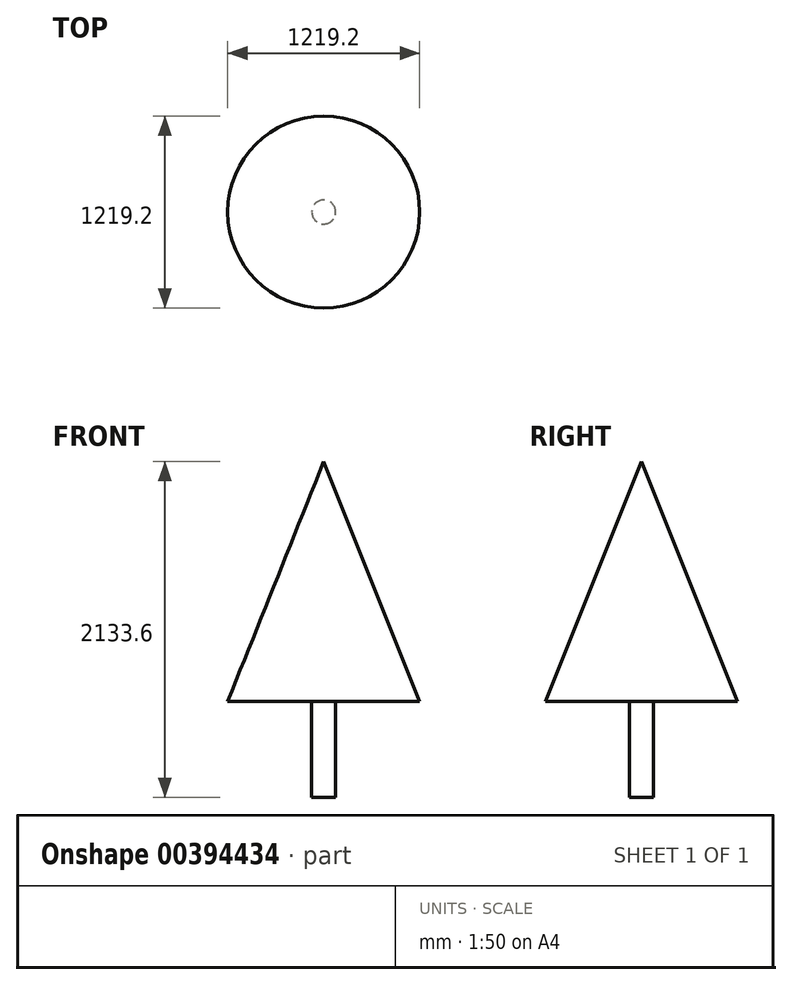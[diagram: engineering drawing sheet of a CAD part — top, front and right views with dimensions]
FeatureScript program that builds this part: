
annotation { "Feature Type Name" : "Feature", "Feature Type Description" : "" }
export const myFeature = defineFeature(function(context is Context, id is Id, definition is map)
    precondition{}
    {
        {
            var Q0;
            Q0=qCreatedBy(makeId("Top.planeOp"),FACE);
            var sketch = newSketch(context, id + "F0", { "sketchPlane" : qUnion([Q0])});
            skCircle(sketch, "E0", {"center": v(0, 0) * mm, "radius": 609.6 * mm});
            skSolve(sketch);
        }
        {
            var Q0;
            Q0=qCreatedBy(makeId("Front.planeOp"),FACE);
            var sketch = newSketch(context, id + "F1", { "sketchPlane" : qUnion([Q0])});
            skLineSegment(sketch, "E1", {"start": v(0, 0) * mm, "end": v(0, 1524) * mm});
            skSolve(sketch);
        }
        {
            var Q0;
            Q0=makeQuery(id+"F0.imprint","IMPRINT",FACE,{"disambiguationData":[TD([[makeQuery(id+"F0.imprint","IMPRINT",EDGE,{"derivedFrom":sQuery(id+"F0.wireOp",EDGE,"E0")}),1.0]])]});
            var Q1;
            Q1=sQuery(id+"F1.wireOp",VERTEX,"E1.end");
            loft(context, id + "F2", {"sheetProfilesArray" : [{ "sheetProfileEntities" : qUnion([Q0]) }, { "sheetProfileEntities" : qUnion([Q1]) }]});
        }
        {
            var Q0;
            Q0=makeQuery(id+"F2.opLoft","CAP_FACE",FACE,{"disambiguationData":[OSD([makeQuery(id+"F0.imprint","IMPRINT",FACE,{"disambiguationData":[TD([[makeQuery(id+"F0.imprint","IMPRINT",EDGE,{"derivedFrom":sQuery(id+"F0.wireOp",EDGE,"E0")}),1.0]])]})])],"isStart":true});
            var sketch = newSketch(context, id + "F3", { "sketchPlane" : qUnion([Q0])});
            skCircle(sketch, "E2", {"center": v(0, 0) * mm, "radius": 76.2 * mm});
            skSolve(sketch);
        }
        {
            var Q0;
            Q0=makeQuery(id+"F3.imprint","IMPRINT",FACE,{"disambiguationData":[TD([[makeQuery(id+"F3.imprint","IMPRINT",EDGE,{"derivedFrom":sQuery(id+"F3.wireOp",EDGE,"E2")}),1.0]])]});
            extrude(context, id + "F4", {"entities" : qUnion([Q0]), "operationType" : NewBodyOperationType.ADD, "depth" : 609.6 * mm});
        }
    });
